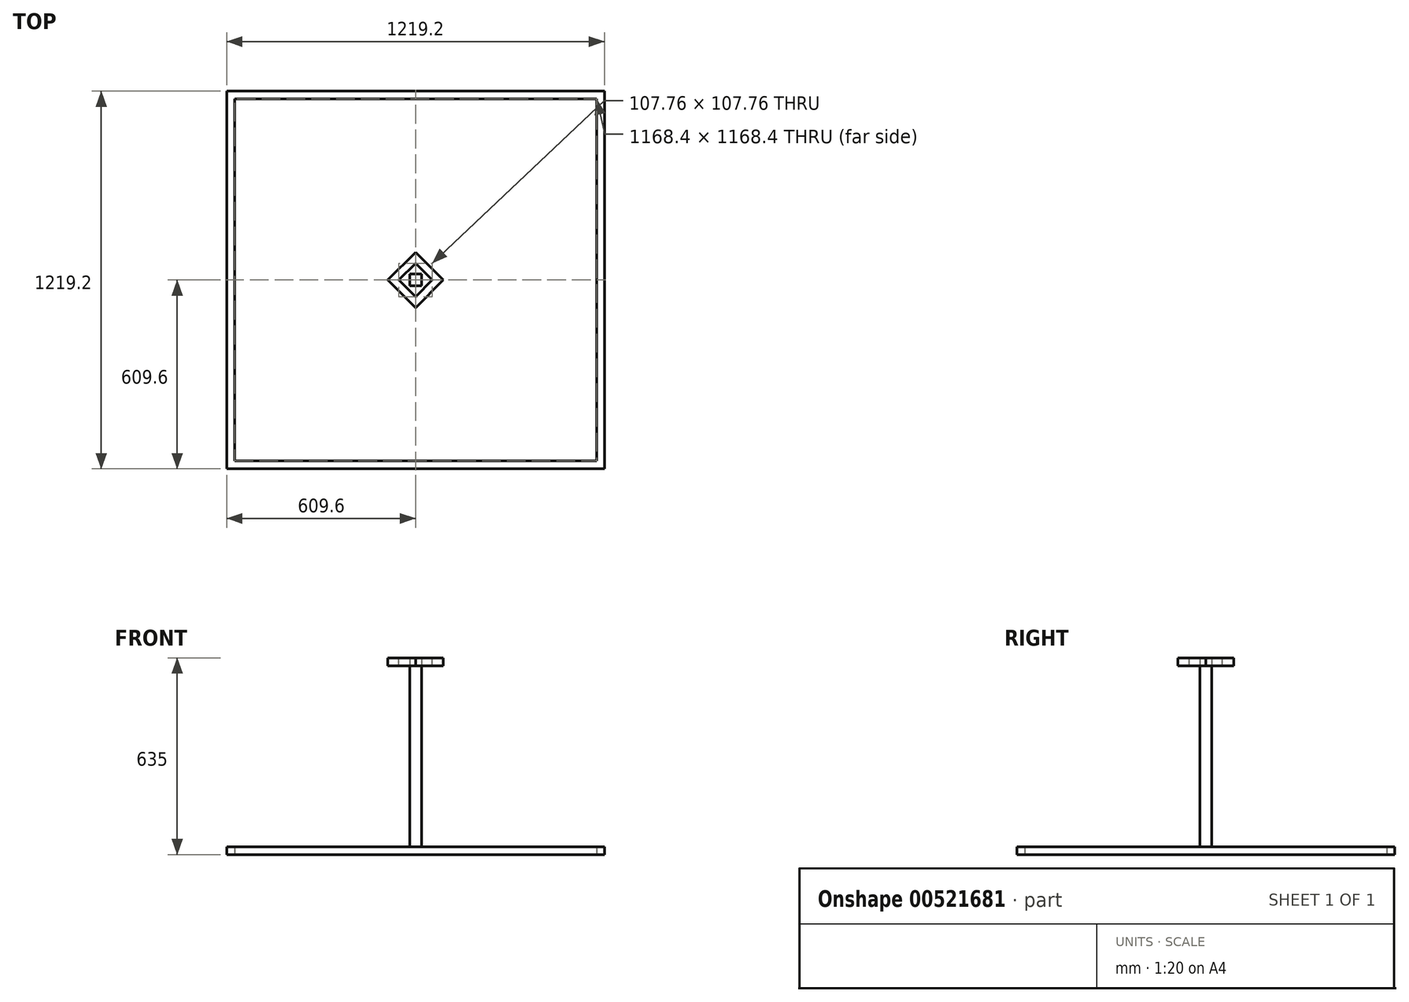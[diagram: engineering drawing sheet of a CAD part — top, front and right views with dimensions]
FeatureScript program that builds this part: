
annotation { "Feature Type Name" : "Feature", "Feature Type Description" : "" }
export const myFeature = defineFeature(function(context is Context, id is Id, definition is map)
    precondition{}
    {
        {
            var Q0;
            Q0=qCreatedBy(makeId("Top.planeOp"),FACE);
            var sketch = newSketch(context, id + "F0", { "sketchPlane" : qUnion([Q0])});
            skLineSegment(sketch, "E0.bottom", {"start": v(-609.6, 609.6) * mm, "end": v(609.6, 609.6) * mm});
            skLineSegment(sketch, "E0.top", {"start": v(-609.6, -609.6) * mm, "end": v(609.6, -609.6) * mm});
            skLineSegment(sketch, "E0.left", {"start": v(-609.6, 609.6) * mm, "end": v(-609.6, -609.6) * mm});
            skLineSegment(sketch, "E0.right", {"start": v(609.6, 609.6) * mm, "end": v(609.6, -609.6) * mm});
            skPoint(sketch, "E0.middle", {"position": v(0, 0) * mm});
            skLineSegment(sketch, "E1.bottom", {"start": v(-584.2, -584.2) * mm, "end": v(584.2, -584.2) * mm});
            skLineSegment(sketch, "E1.top", {"start": v(-584.2, 584.2) * mm, "end": v(584.2, 584.2) * mm});
            skLineSegment(sketch, "E1.left", {"start": v(-584.2, -584.2) * mm, "end": v(-584.2, 584.2) * mm});
            skLineSegment(sketch, "E1.right", {"start": v(584.2, -584.2) * mm, "end": v(584.2, 584.2) * mm});
            skLineSegment(sketch, "E2.bottom", {"start": v(-12.7, 584.2) * mm, "end": v(12.7, 584.2) * mm});
            skLineSegment(sketch, "E2.top", {"start": v(-12.7, -584.2) * mm, "end": v(12.7, -584.2) * mm});
            skLineSegment(sketch, "E2.left", {"start": v(-12.7, 584.2) * mm, "end": v(-12.7, -584.2) * mm});
            skLineSegment(sketch, "E2.right", {"start": v(12.7, 584.2) * mm, "end": v(12.7, -584.2) * mm});
            skSolve(sketch);
        }
        {
            var Q0;
            Q0=makeQuery(id+"F0.imprint","IMPRINT",FACE,{"disambiguationData":[TD([[makeQuery(id+"F0.imprint","IMPRINT",EDGE,{"derivedFrom":sQuery(id+"F0.wireOp",EDGE,"E0.bottom")}),-1.0]])]});
            var Q1;
            Q1=makeQuery(id+"F0.imprint","IMPRINT",FACE,{"disambiguationData":[TD([[makeQuery(id+"F0.imprint","IMPRINT",EDGE,{"derivedFrom":sQuery(id+"F0.wireOp",EDGE,"E2.bottom")}),-1.0]])]});
            extrude(context, id + "F1", {"entities" : qUnion([Q0, Q1]), "depth" : 25.4 * mm, "offsetDistance" : 25.4 * mm});
        }
        {
            var Q0;
            Q0=makeQuery(id+"F1.opExtrude","CAP_FACE",FACE,{"disambiguationData":[OSD([sQuery(id+"F0.wireOp",EDGE,"E0.bottom"),sQuery(id+"F0.wireOp",EDGE,"E0.top"),sQuery(id+"F0.wireOp",EDGE,"E0.left"),sQuery(id+"F0.wireOp",EDGE,"E0.right"),sQuery(id+"F0.wireOp",EDGE,"E1.bottom"),sQuery(id+"F0.wireOp",EDGE,"E1.top"),sQuery(id+"F0.wireOp",EDGE,"E1.left"),sQuery(id+"F0.wireOp",EDGE,"E1.right"),sQuery(id+"F0.wireOp",EDGE,"E2.left"),sQuery(id+"F0.wireOp",EDGE,"E2.right")])],"isStart":false});
            var sketch = newSketch(context, id + "F2", { "sketchPlane" : qUnion([Q0])});
            skLineSegment(sketch, "E3.bottom", {"start": v(-38.1, 38.1) * mm, "end": v(38.1, 38.1) * mm});
            skLineSegment(sketch, "E3.top", {"start": v(-38.1, -38.1) * mm, "end": v(38.1, -38.1) * mm});
            skLineSegment(sketch, "E3.left", {"start": v(-38.1, 38.1) * mm, "end": v(-38.1, -38.1) * mm});
            skLineSegment(sketch, "E3.right", {"start": v(38.1, 38.1) * mm, "end": v(38.1, -38.1) * mm});
            skPoint(sketch, "E3.middle", {"position": v(0, 0) * mm});
            skLineSegment(sketch, "E4.bottom", {"start": v(-63.5, 63.5) * mm, "end": v(63.5, 63.5) * mm});
            skLineSegment(sketch, "E4.top", {"start": v(-63.5, -63.5) * mm, "end": v(63.5, -63.5) * mm});
            skLineSegment(sketch, "E4.left", {"start": v(-63.5, 63.5) * mm, "end": v(-63.5, -63.5) * mm});
            skLineSegment(sketch, "E4.right", {"start": v(63.5, 63.5) * mm, "end": v(63.5, -63.5) * mm});
            skSolve(sketch);
        }
        {
            var Q0;
            Q0=makeQuery(id+"F1.opExtrude","CAP_FACE",FACE,{"disambiguationData":[OSD([sQuery(id+"F0.wireOp",EDGE,"E0.bottom"),sQuery(id+"F0.wireOp",EDGE,"E0.top"),sQuery(id+"F0.wireOp",EDGE,"E0.left"),sQuery(id+"F0.wireOp",EDGE,"E0.right"),sQuery(id+"F0.wireOp",EDGE,"E1.bottom"),sQuery(id+"F0.wireOp",EDGE,"E1.top"),sQuery(id+"F0.wireOp",EDGE,"E1.left"),sQuery(id+"F0.wireOp",EDGE,"E1.right"),sQuery(id+"F0.wireOp",EDGE,"E2.left"),sQuery(id+"F0.wireOp",EDGE,"E2.right")])],"isStart":false});
            var sketch = newSketch(context, id + "F3", { "sketchPlane" : qUnion([Q0])});
            skLineSegment(sketch, "E5.bottom", {"start": v(19.05, 19.05) * mm, "end": v(-19.05, 19.05) * mm});
            skLineSegment(sketch, "E5.top", {"start": v(19.05, -19.05) * mm, "end": v(-19.05, -19.05) * mm});
            skLineSegment(sketch, "E5.left", {"start": v(19.05, 19.05) * mm, "end": v(19.05, -19.05) * mm});
            skLineSegment(sketch, "E5.right", {"start": v(-19.05, 19.05) * mm, "end": v(-19.05, -19.05) * mm});
            skPoint(sketch, "E5.middle", {"position": v(0, 0) * mm});
            skSolve(sketch);
        }
        {
            var Q0;
            Q0 = qSketchRegion(id + "F3", true);
            extrude(context, id + "F4", {"entities" : qUnion([Q0]), "operationType" : NewBodyOperationType.ADD, "depth" : 609.6 * mm, "offsetDistance" : 25.4 * mm});
        }
        {
            var Q0;
            Q0=makeQuery(id+"F4.opExtrude","CAP_FACE",FACE,{"disambiguationData":[OSD([sQuery(id+"F3.wireOp",EDGE,"E5.bottom"),sQuery(id+"F3.wireOp",EDGE,"E5.top"),sQuery(id+"F3.wireOp",EDGE,"E5.left"),sQuery(id+"F3.wireOp",EDGE,"E5.right")])],"isStart":false});
            var sketch = newSketch(context, id + "F5", { "sketchPlane" : qUnion([Q0])});
            skLineSegment(sketch, "E6.bottom", {"start": v(-53.88, 0) * mm, "end": v(0, 53.88) * mm});
            skLineSegment(sketch, "E6.top", {"start": v(0, -53.88) * mm, "end": v(53.88, 0) * mm});
            skLineSegment(sketch, "E6.left", {"start": v(-53.88, 0) * mm, "end": v(0, -53.88) * mm});
            skLineSegment(sketch, "E6.right", {"start": v(0, 53.88) * mm, "end": v(53.88, 0) * mm});
            skPoint(sketch, "E6.middle", {"position": v(0, 0) * mm});
            skLineSegment(sketch, "E7.bottom", {"start": v(0, 89.8) * mm, "end": v(89.8, 0) * mm});
            skLineSegment(sketch, "E7.top", {"start": v(-89.8, 0) * mm, "end": v(0, -89.8) * mm});
            skLineSegment(sketch, "E7.left", {"start": v(0, 89.8) * mm, "end": v(-89.8, 0) * mm});
            skLineSegment(sketch, "E7.right", {"start": v(89.8, 0) * mm, "end": v(0, -89.8) * mm});
            skSolve(sketch);
        }
        {
            var Q0;
            Q0=makeQuery(id+"F5.imprint","IMPRINT",FACE,{"disambiguationData":[TD([[makeQuery(id+"F5.imprint","IMPRINT",EDGE,{"derivedFrom":sQuery(id+"F5.wireOp",EDGE,"E6.bottom")}),1.0]])]});
            extrude(context, id + "F6", {"entities" : qUnion([Q0]), "oppositeDirection" : true, "depth" : 25.4 * mm, "offsetDistance" : 25.4 * mm});
        }
    });
